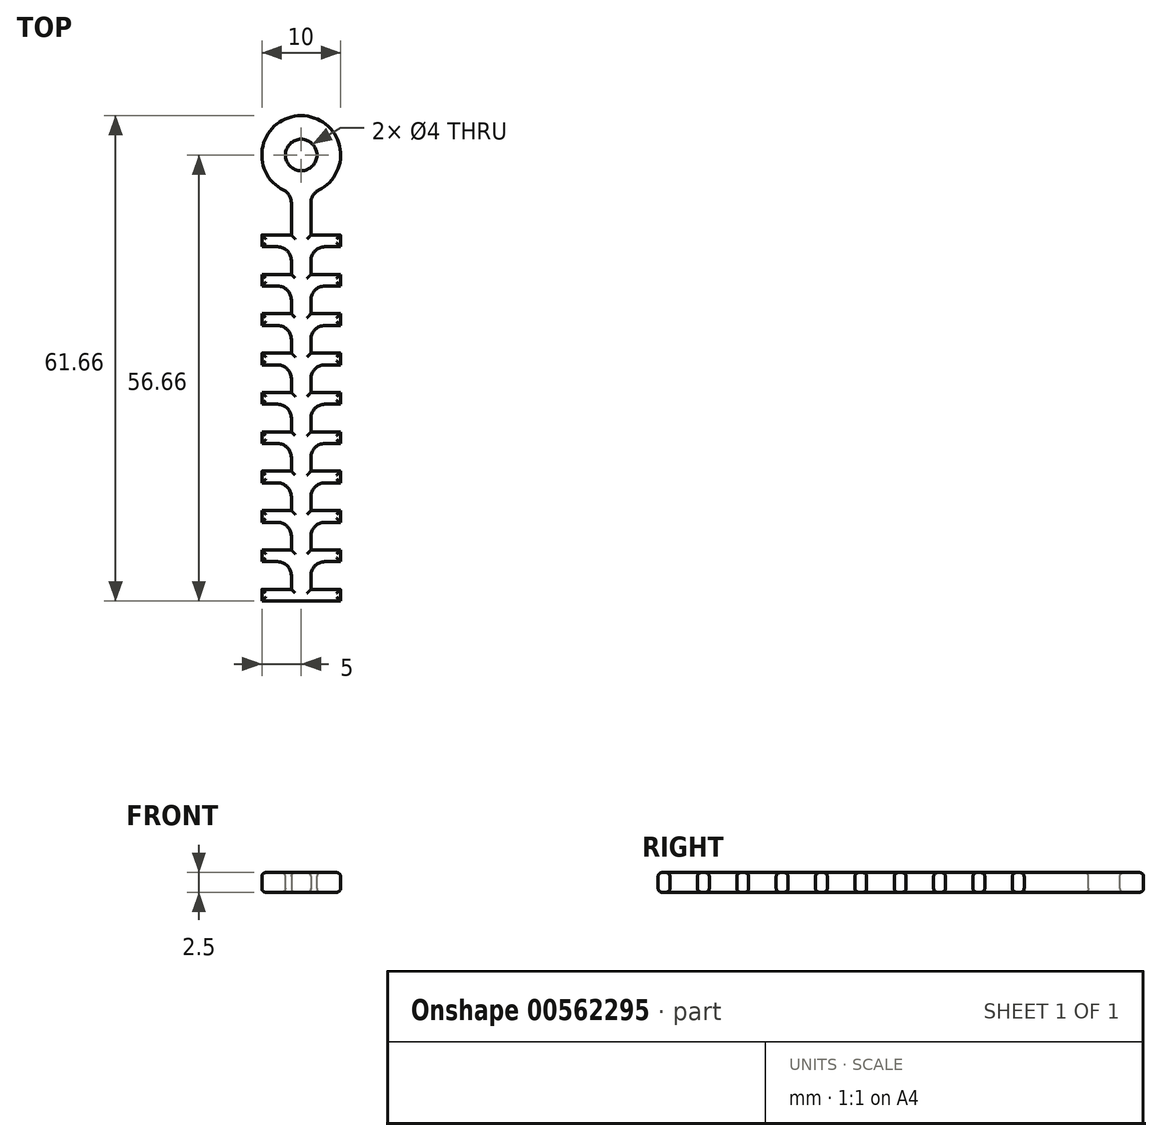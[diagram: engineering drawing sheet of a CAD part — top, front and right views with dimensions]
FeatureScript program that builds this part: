
annotation { "Feature Type Name" : "Feature", "Feature Type Description" : "" }
export const myFeature = defineFeature(function(context is Context, id is Id, definition is map)
    precondition{}
    {
        {
            var Q0;
            Q0=qCreatedBy(makeId("Top.planeOp"),FACE);
            var sketch = newSketch(context, id + "F0", { "sketchPlane" : qUnion([Q0])});
            skCircle(sketch, "E0", {"center": v(0, 0) * mm, "radius": 5 * mm});
            skLineSegment(sketch, "E1.bottom", {"start": v(5, -11.66) * mm, "end": v(-5, -11.66) * mm});
            skLineSegment(sketch, "E1.top", {"start": v(5, -10.16) * mm, "end": v(-5, -10.16) * mm});
            skLineSegment(sketch, "E1.left", {"start": v(5, -11.66) * mm, "end": v(5, -10.16) * mm});
            skLineSegment(sketch, "E1.right", {"start": v(-5, -11.66) * mm, "end": v(-5, -10.16) * mm});
            skPoint(sketch, "E1.middle", {"position": v(0, -10.91) * mm});
            skPoint(sketch, "E2.0.1.0", {"position": v(0, -15.91) * mm});
            skLineSegment(sketch, "E2.0.1.1", {"start": v(-5, -16.66) * mm, "end": v(-5, -15.16) * mm});
            skLineSegment(sketch, "E2.0.1.2", {"start": v(5, -16.66) * mm, "end": v(5, -15.16) * mm});
            skLineSegment(sketch, "E2.0.1.3", {"start": v(5, -15.16) * mm, "end": v(-5, -15.16) * mm});
            skLineSegment(sketch, "E2.0.1.4", {"start": v(5, -16.66) * mm, "end": v(-5, -16.66) * mm});
            skPoint(sketch, "E2.0.2.0", {"position": v(0, -20.91) * mm});
            skLineSegment(sketch, "E2.0.2.1", {"start": v(-5, -21.66) * mm, "end": v(-5, -20.16) * mm});
            skLineSegment(sketch, "E2.0.2.2", {"start": v(5, -21.66) * mm, "end": v(5, -20.16) * mm});
            skLineSegment(sketch, "E2.0.2.3", {"start": v(5, -20.16) * mm, "end": v(-5, -20.16) * mm});
            skLineSegment(sketch, "E2.0.2.4", {"start": v(5, -21.66) * mm, "end": v(-5, -21.66) * mm});
            skPoint(sketch, "E2.0.3.0", {"position": v(0, -25.91) * mm});
            skLineSegment(sketch, "E2.0.3.1", {"start": v(-5, -26.66) * mm, "end": v(-5, -25.16) * mm});
            skLineSegment(sketch, "E2.0.3.2", {"start": v(5, -26.66) * mm, "end": v(5, -25.16) * mm});
            skLineSegment(sketch, "E2.0.3.3", {"start": v(5, -25.16) * mm, "end": v(-5, -25.16) * mm});
            skLineSegment(sketch, "E2.0.3.4", {"start": v(5, -26.66) * mm, "end": v(-5, -26.66) * mm});
            skPoint(sketch, "E2.0.4.0", {"position": v(0, -30.91) * mm});
            skLineSegment(sketch, "E2.0.4.1", {"start": v(-5, -31.66) * mm, "end": v(-5, -30.16) * mm});
            skLineSegment(sketch, "E2.0.4.2", {"start": v(5, -31.66) * mm, "end": v(5, -30.16) * mm});
            skLineSegment(sketch, "E2.0.4.3", {"start": v(5, -30.16) * mm, "end": v(-5, -30.16) * mm});
            skLineSegment(sketch, "E2.0.4.4", {"start": v(5, -31.66) * mm, "end": v(-5, -31.66) * mm});
            skPoint(sketch, "E2.0.5.0", {"position": v(0, -35.91) * mm});
            skLineSegment(sketch, "E2.0.5.1", {"start": v(-5, -36.66) * mm, "end": v(-5, -35.16) * mm});
            skLineSegment(sketch, "E2.0.5.2", {"start": v(5, -36.66) * mm, "end": v(5, -35.16) * mm});
            skLineSegment(sketch, "E2.0.5.3", {"start": v(5, -35.16) * mm, "end": v(-5, -35.16) * mm});
            skLineSegment(sketch, "E2.0.5.4", {"start": v(5, -36.66) * mm, "end": v(-5, -36.66) * mm});
            skPoint(sketch, "E2.0.6.0", {"position": v(0, -40.91) * mm});
            skLineSegment(sketch, "E2.0.6.1", {"start": v(-5, -41.66) * mm, "end": v(-5, -40.16) * mm});
            skLineSegment(sketch, "E2.0.6.2", {"start": v(5, -41.66) * mm, "end": v(5, -40.16) * mm});
            skLineSegment(sketch, "E2.0.6.3", {"start": v(5, -40.16) * mm, "end": v(-5, -40.16) * mm});
            skLineSegment(sketch, "E2.0.6.4", {"start": v(5, -41.66) * mm, "end": v(-5, -41.66) * mm});
            skPoint(sketch, "E2.0.7.0", {"position": v(0, -45.91) * mm});
            skLineSegment(sketch, "E2.0.7.1", {"start": v(-5, -46.66) * mm, "end": v(-5, -45.16) * mm});
            skLineSegment(sketch, "E2.0.7.2", {"start": v(5, -46.66) * mm, "end": v(5, -45.16) * mm});
            skLineSegment(sketch, "E2.0.7.3", {"start": v(5, -45.16) * mm, "end": v(-5, -45.16) * mm});
            skLineSegment(sketch, "E2.0.7.4", {"start": v(5, -46.66) * mm, "end": v(-5, -46.66) * mm});
            skPoint(sketch, "E2.0.8.0", {"position": v(0, -50.91) * mm});
            skLineSegment(sketch, "E2.0.8.1", {"start": v(-5, -51.66) * mm, "end": v(-5, -50.16) * mm});
            skLineSegment(sketch, "E2.0.8.2", {"start": v(5, -51.66) * mm, "end": v(5, -50.16) * mm});
            skLineSegment(sketch, "E2.0.8.3", {"start": v(5, -50.16) * mm, "end": v(-5, -50.16) * mm});
            skLineSegment(sketch, "E2.0.8.4", {"start": v(5, -51.66) * mm, "end": v(-5, -51.66) * mm});
            skPoint(sketch, "E2.0.9.0", {"position": v(0, -55.91) * mm});
            skLineSegment(sketch, "E2.0.9.1", {"start": v(-5, -56.66) * mm, "end": v(-5, -55.16) * mm});
            skLineSegment(sketch, "E2.0.9.2", {"start": v(5, -56.66) * mm, "end": v(5, -55.16) * mm});
            skLineSegment(sketch, "E2.0.9.3", {"start": v(5, -55.16) * mm, "end": v(-5, -55.16) * mm});
            skLineSegment(sketch, "E2.0.9.4", {"start": v(5, -56.66) * mm, "end": v(-5, -56.66) * mm});
            skLineSegment(sketch, "E2.direction1", {"start": v(-5, -11.66) * mm, "end": v(12.1, -11.66) * mm, "construction": true});
            skLineSegment(sketch, "E2.direction2", {"start": v(-5, -11.66) * mm, "end": v(-5, -16.66) * mm, "construction": true});
            skLineSegment(sketch, "E3.bottom", {"start": v(-1.25, -55.16) * mm, "end": v(1.25, -55.16) * mm});
            skLineSegment(sketch, "E3.top", {"start": v(-1.25, -4.84) * mm, "end": v(1.25, -4.84) * mm});
            skLineSegment(sketch, "E3.left", {"start": v(-1.25, -55.16) * mm, "end": v(-1.25, -4.84) * mm});
            skLineSegment(sketch, "E3.right", {"start": v(1.25, -55.16) * mm, "end": v(1.25, -4.84) * mm});
            skSolve(sketch);
        }
        {
            var Q0;
            Q0 = qSketchRegion(id + "F0", true);
            extrude(context, id + "F1", {"entities" : qUnion([Q0]), "depth" : 2.5 * mm, "offsetDistance" : 25 * mm});
        }
        {
            var Q0;
            Q0=makeQuery(id+"F1.opExtrude","CAP_FACE",FACE,{"disambiguationData":[OSD([sQuery(id+"F0.wireOp",EDGE,"E0"),sQuery(id+"F0.wireOp",EDGE,"E1.bottom"),sQuery(id+"F0.wireOp",EDGE,"E1.top"),sQuery(id+"F0.wireOp",EDGE,"E1.left"),sQuery(id+"F0.wireOp",EDGE,"E1.right"),sQuery(id+"F0.wireOp",EDGE,"E2.0.1.1"),sQuery(id+"F0.wireOp",EDGE,"E2.0.1.2"),sQuery(id+"F0.wireOp",EDGE,"E2.0.1.3"),sQuery(id+"F0.wireOp",EDGE,"E2.0.1.4"),sQuery(id+"F0.wireOp",EDGE,"E2.0.2.1"),sQuery(id+"F0.wireOp",EDGE,"E2.0.2.2"),sQuery(id+"F0.wireOp",EDGE,"E2.0.2.3"),sQuery(id+"F0.wireOp",EDGE,"E2.0.2.4"),sQuery(id+"F0.wireOp",EDGE,"E2.0.3.1"),sQuery(id+"F0.wireOp",EDGE,"E2.0.3.2"),sQuery(id+"F0.wireOp",EDGE,"E2.0.3.3"),sQuery(id+"F0.wireOp",EDGE,"E2.0.3.4"),sQuery(id+"F0.wireOp",EDGE,"E2.0.4.1"),sQuery(id+"F0.wireOp",EDGE,"E2.0.4.2"),sQuery(id+"F0.wireOp",EDGE,"E2.0.4.3"),sQuery(id+"F0.wireOp",EDGE,"E2.0.4.4"),sQuery(id+"F0.wireOp",EDGE,"E2.0.5.1"),sQuery(id+"F0.wireOp",EDGE,"E2.0.5.2"),sQuery(id+"F0.wireOp",EDGE,"E2.0.5.3"),sQuery(id+"F0.wireOp",EDGE,"E2.0.5.4"),sQuery(id+"F0.wireOp",EDGE,"E2.0.6.1"),sQuery(id+"F0.wireOp",EDGE,"E2.0.6.2"),sQuery(id+"F0.wireOp",EDGE,"E2.0.6.3"),sQuery(id+"F0.wireOp",EDGE,"E2.0.6.4"),sQuery(id+"F0.wireOp",EDGE,"E2.0.7.1"),sQuery(id+"F0.wireOp",EDGE,"E2.0.7.2"),sQuery(id+"F0.wireOp",EDGE,"E2.0.7.3"),sQuery(id+"F0.wireOp",EDGE,"E2.0.7.4"),sQuery(id+"F0.wireOp",EDGE,"E2.0.8.1"),sQuery(id+"F0.wireOp",EDGE,"E2.0.8.2"),sQuery(id+"F0.wireOp",EDGE,"E2.0.8.3"),sQuery(id+"F0.wireOp",EDGE,"E2.0.8.4"),sQuery(id+"F0.wireOp",EDGE,"E2.0.9.1"),sQuery(id+"F0.wireOp",EDGE,"E2.0.9.2"),sQuery(id+"F0.wireOp",EDGE,"E2.0.9.3"),sQuery(id+"F0.wireOp",EDGE,"E2.0.9.4"),sQuery(id+"F0.wireOp",EDGE,"E3.left"),sQuery(id+"F0.wireOp",EDGE,"E3.right")])],"isStart":false});
            var sketch = newSketch(context, id + "F2", { "sketchPlane" : qUnion([Q0])});
            skCircle(sketch, "E4", {"center": v(0, 0) * mm, "radius": 2 * mm});
            skSolve(sketch);
        }
        {
            var Q0;
            Q0 = qSketchRegion(id + "F2", true);
            var Q1;
            Q1=makeQuery(id+"F1.opExtrude","CAP_FACE",FACE,{"disambiguationData":[OSD([sQuery(id+"F0.wireOp",EDGE,"E0"),sQuery(id+"F0.wireOp",EDGE,"E1.bottom"),sQuery(id+"F0.wireOp",EDGE,"E1.top"),sQuery(id+"F0.wireOp",EDGE,"E1.left"),sQuery(id+"F0.wireOp",EDGE,"E1.right"),sQuery(id+"F0.wireOp",EDGE,"E2.0.1.1"),sQuery(id+"F0.wireOp",EDGE,"E2.0.1.2"),sQuery(id+"F0.wireOp",EDGE,"E2.0.1.3"),sQuery(id+"F0.wireOp",EDGE,"E2.0.1.4"),sQuery(id+"F0.wireOp",EDGE,"E2.0.2.1"),sQuery(id+"F0.wireOp",EDGE,"E2.0.2.2"),sQuery(id+"F0.wireOp",EDGE,"E2.0.2.3"),sQuery(id+"F0.wireOp",EDGE,"E2.0.2.4"),sQuery(id+"F0.wireOp",EDGE,"E2.0.3.1"),sQuery(id+"F0.wireOp",EDGE,"E2.0.3.2"),sQuery(id+"F0.wireOp",EDGE,"E2.0.3.3"),sQuery(id+"F0.wireOp",EDGE,"E2.0.3.4"),sQuery(id+"F0.wireOp",EDGE,"E2.0.4.1"),sQuery(id+"F0.wireOp",EDGE,"E2.0.4.2"),sQuery(id+"F0.wireOp",EDGE,"E2.0.4.3"),sQuery(id+"F0.wireOp",EDGE,"E2.0.4.4"),sQuery(id+"F0.wireOp",EDGE,"E2.0.5.1"),sQuery(id+"F0.wireOp",EDGE,"E2.0.5.2"),sQuery(id+"F0.wireOp",EDGE,"E2.0.5.3"),sQuery(id+"F0.wireOp",EDGE,"E2.0.5.4"),sQuery(id+"F0.wireOp",EDGE,"E2.0.6.1"),sQuery(id+"F0.wireOp",EDGE,"E2.0.6.2"),sQuery(id+"F0.wireOp",EDGE,"E2.0.6.3"),sQuery(id+"F0.wireOp",EDGE,"E2.0.6.4"),sQuery(id+"F0.wireOp",EDGE,"E2.0.7.1"),sQuery(id+"F0.wireOp",EDGE,"E2.0.7.2"),sQuery(id+"F0.wireOp",EDGE,"E2.0.7.3"),sQuery(id+"F0.wireOp",EDGE,"E2.0.7.4"),sQuery(id+"F0.wireOp",EDGE,"E2.0.8.1"),sQuery(id+"F0.wireOp",EDGE,"E2.0.8.2"),sQuery(id+"F0.wireOp",EDGE,"E2.0.8.3"),sQuery(id+"F0.wireOp",EDGE,"E2.0.8.4"),sQuery(id+"F0.wireOp",EDGE,"E2.0.9.1"),sQuery(id+"F0.wireOp",EDGE,"E2.0.9.2"),sQuery(id+"F0.wireOp",EDGE,"E2.0.9.3"),sQuery(id+"F0.wireOp",EDGE,"E2.0.9.4"),sQuery(id+"F0.wireOp",EDGE,"E3.left"),sQuery(id+"F0.wireOp",EDGE,"E3.right")])],"isStart":true});
            extrude(context, id + "F3", {"entities" : qUnion([Q0]), "operationType" : NewBodyOperationType.REMOVE, "endBound" : BoundingType.UP_TO_SURFACE, "oppositeDirection" : true, "depth" : 25 * mm, "endBoundEntityFace" : qUnion([Q1]), "offsetDistance" : 25 * mm});
        }
        {
            var Q0;
            Q0=makeQuery(id+"F1.opExtrude","SWEPT_EDGE",EDGE,{"disambiguationData":[OSD([sQuery(id+"F0.wireOp",EDGE,"E0"),sQuery(id+"F0.wireOp",EDGE,"E3.top"),sQuery(id+"F0.wireOp",EDGE,"E3.right")])]});
            var Q1;
            Q1=makeQuery(id+"F1.opExtrude","SWEPT_EDGE",EDGE,{"disambiguationData":[OSD([sQuery(id+"F0.wireOp",EDGE,"E0"),sQuery(id+"F0.wireOp",EDGE,"E3.top"),sQuery(id+"F0.wireOp",EDGE,"E3.left")])]});
            var Q2;
            Q2=makeQuery(id+"F1.opExtrude","SWEPT_EDGE",EDGE,{"disambiguationData":[OSD([sQuery(id+"F0.wireOp",EDGE,"E1.bottom"),sQuery(id+"F0.wireOp",EDGE,"E3.right")])]});
            var Q3;
            Q3=makeQuery(id+"F1.opExtrude","SWEPT_EDGE",EDGE,{"disambiguationData":[OSD([sQuery(id+"F0.wireOp",EDGE,"E2.0.1.4"),sQuery(id+"F0.wireOp",EDGE,"E3.right")])]});
            var Q4;
            Q4=makeQuery(id+"F1.opExtrude","SWEPT_EDGE",EDGE,{"disambiguationData":[OSD([sQuery(id+"F0.wireOp",EDGE,"E2.0.2.4"),sQuery(id+"F0.wireOp",EDGE,"E3.right")])]});
            var Q5;
            Q5=makeQuery(id+"F1.opExtrude","SWEPT_EDGE",EDGE,{"disambiguationData":[OSD([sQuery(id+"F0.wireOp",EDGE,"E2.0.3.4"),sQuery(id+"F0.wireOp",EDGE,"E3.right")])]});
            var Q6;
            Q6=makeQuery(id+"F1.opExtrude","SWEPT_EDGE",EDGE,{"disambiguationData":[OSD([sQuery(id+"F0.wireOp",EDGE,"E2.0.4.4"),sQuery(id+"F0.wireOp",EDGE,"E3.right")])]});
            var Q7;
            Q7=makeQuery(id+"F1.opExtrude","SWEPT_EDGE",EDGE,{"disambiguationData":[OSD([sQuery(id+"F0.wireOp",EDGE,"E2.0.5.4"),sQuery(id+"F0.wireOp",EDGE,"E3.right")])]});
            var Q8;
            Q8=makeQuery(id+"F1.opExtrude","SWEPT_EDGE",EDGE,{"disambiguationData":[OSD([sQuery(id+"F0.wireOp",EDGE,"E2.0.6.4"),sQuery(id+"F0.wireOp",EDGE,"E3.right")])]});
            var Q9;
            Q9=makeQuery(id+"F1.opExtrude","SWEPT_EDGE",EDGE,{"disambiguationData":[OSD([sQuery(id+"F0.wireOp",EDGE,"E2.0.7.4"),sQuery(id+"F0.wireOp",EDGE,"E3.right")])]});
            var Q10;
            Q10=makeQuery(id+"F1.opExtrude","SWEPT_EDGE",EDGE,{"disambiguationData":[OSD([sQuery(id+"F0.wireOp",EDGE,"E2.0.8.4"),sQuery(id+"F0.wireOp",EDGE,"E3.right")])]});
            var Q11;
            Q11=makeQuery(id+"F1.opExtrude","SWEPT_EDGE",EDGE,{"disambiguationData":[OSD([sQuery(id+"F0.wireOp",EDGE,"E2.0.8.4"),sQuery(id+"F0.wireOp",EDGE,"E3.left")])]});
            var Q12;
            Q12=makeQuery(id+"F1.opExtrude","SWEPT_EDGE",EDGE,{"disambiguationData":[OSD([sQuery(id+"F0.wireOp",EDGE,"E2.0.7.4"),sQuery(id+"F0.wireOp",EDGE,"E3.left")])]});
            var Q13;
            Q13=makeQuery(id+"F1.opExtrude","SWEPT_EDGE",EDGE,{"disambiguationData":[OSD([sQuery(id+"F0.wireOp",EDGE,"E2.0.6.4"),sQuery(id+"F0.wireOp",EDGE,"E3.left")])]});
            var Q14;
            Q14=makeQuery(id+"F1.opExtrude","SWEPT_EDGE",EDGE,{"disambiguationData":[OSD([sQuery(id+"F0.wireOp",EDGE,"E2.0.5.4"),sQuery(id+"F0.wireOp",EDGE,"E3.left")])]});
            var Q15;
            Q15=makeQuery(id+"F1.opExtrude","SWEPT_EDGE",EDGE,{"disambiguationData":[OSD([sQuery(id+"F0.wireOp",EDGE,"E2.0.4.4"),sQuery(id+"F0.wireOp",EDGE,"E3.left")])]});
            var Q16;
            Q16=makeQuery(id+"F1.opExtrude","SWEPT_EDGE",EDGE,{"disambiguationData":[OSD([sQuery(id+"F0.wireOp",EDGE,"E2.0.3.4"),sQuery(id+"F0.wireOp",EDGE,"E3.left")])]});
            var Q17;
            Q17=makeQuery(id+"F1.opExtrude","SWEPT_EDGE",EDGE,{"disambiguationData":[OSD([sQuery(id+"F0.wireOp",EDGE,"E2.0.2.4"),sQuery(id+"F0.wireOp",EDGE,"E3.left")])]});
            var Q18;
            Q18=makeQuery(id+"F1.opExtrude","SWEPT_EDGE",EDGE,{"disambiguationData":[OSD([sQuery(id+"F0.wireOp",EDGE,"E2.0.1.4"),sQuery(id+"F0.wireOp",EDGE,"E3.left")])]});
            var Q19;
            Q19=makeQuery(id+"F1.opExtrude","SWEPT_EDGE",EDGE,{"disambiguationData":[OSD([sQuery(id+"F0.wireOp",EDGE,"E1.bottom"),sQuery(id+"F0.wireOp",EDGE,"E3.left")])]});
            fillet(context, id + "F4", {"entities" : qUnion([Q0, Q1, Q2, Q3, Q4, Q5, Q6, Q7, Q8, Q9, Q10, Q11, Q12, Q13, Q14, Q15, Q16, Q17, Q18, Q19]), "radius" : 1.75 * mm, "tangentPropagation" : true, "allowEdgeOverflow" : false});
        }
        {
            var Q0;
            Q0=makeQuery(id+"F1.opExtrude","CAP_FACE",FACE,{"disambiguationData":[OSD([sQuery(id+"F0.wireOp",EDGE,"E0"),sQuery(id+"F0.wireOp",EDGE,"E1.bottom"),sQuery(id+"F0.wireOp",EDGE,"E1.top"),sQuery(id+"F0.wireOp",EDGE,"E1.left"),sQuery(id+"F0.wireOp",EDGE,"E1.right"),sQuery(id+"F0.wireOp",EDGE,"E2.0.1.1"),sQuery(id+"F0.wireOp",EDGE,"E2.0.1.2"),sQuery(id+"F0.wireOp",EDGE,"E2.0.1.3"),sQuery(id+"F0.wireOp",EDGE,"E2.0.1.4"),sQuery(id+"F0.wireOp",EDGE,"E2.0.2.1"),sQuery(id+"F0.wireOp",EDGE,"E2.0.2.2"),sQuery(id+"F0.wireOp",EDGE,"E2.0.2.3"),sQuery(id+"F0.wireOp",EDGE,"E2.0.2.4"),sQuery(id+"F0.wireOp",EDGE,"E2.0.3.1"),sQuery(id+"F0.wireOp",EDGE,"E2.0.3.2"),sQuery(id+"F0.wireOp",EDGE,"E2.0.3.3"),sQuery(id+"F0.wireOp",EDGE,"E2.0.3.4"),sQuery(id+"F0.wireOp",EDGE,"E2.0.4.1"),sQuery(id+"F0.wireOp",EDGE,"E2.0.4.2"),sQuery(id+"F0.wireOp",EDGE,"E2.0.4.3"),sQuery(id+"F0.wireOp",EDGE,"E2.0.4.4"),sQuery(id+"F0.wireOp",EDGE,"E2.0.5.1"),sQuery(id+"F0.wireOp",EDGE,"E2.0.5.2"),sQuery(id+"F0.wireOp",EDGE,"E2.0.5.3"),sQuery(id+"F0.wireOp",EDGE,"E2.0.5.4"),sQuery(id+"F0.wireOp",EDGE,"E2.0.6.1"),sQuery(id+"F0.wireOp",EDGE,"E2.0.6.2"),sQuery(id+"F0.wireOp",EDGE,"E2.0.6.3"),sQuery(id+"F0.wireOp",EDGE,"E2.0.6.4"),sQuery(id+"F0.wireOp",EDGE,"E2.0.7.1"),sQuery(id+"F0.wireOp",EDGE,"E2.0.7.2"),sQuery(id+"F0.wireOp",EDGE,"E2.0.7.3"),sQuery(id+"F0.wireOp",EDGE,"E2.0.7.4"),sQuery(id+"F0.wireOp",EDGE,"E2.0.8.1"),sQuery(id+"F0.wireOp",EDGE,"E2.0.8.2"),sQuery(id+"F0.wireOp",EDGE,"E2.0.8.3"),sQuery(id+"F0.wireOp",EDGE,"E2.0.8.4"),sQuery(id+"F0.wireOp",EDGE,"E2.0.9.1"),sQuery(id+"F0.wireOp",EDGE,"E2.0.9.2"),sQuery(id+"F0.wireOp",EDGE,"E2.0.9.3"),sQuery(id+"F0.wireOp",EDGE,"E2.0.9.4"),sQuery(id+"F0.wireOp",EDGE,"E3.left"),sQuery(id+"F0.wireOp",EDGE,"E3.right")])],"isStart":false});
            fillet(context, id + "F5", {"entities" : qUnion([Q0]), "radius" : .5 * mm, "tangentPropagation" : true, "allowEdgeOverflow" : false});
        }
        {
            var Q0;
            Q0=makeQuery(id+"F1.opExtrude","CAP_FACE",FACE,{"disambiguationData":[OSD([sQuery(id+"F0.wireOp",EDGE,"E0"),sQuery(id+"F0.wireOp",EDGE,"E1.bottom"),sQuery(id+"F0.wireOp",EDGE,"E1.top"),sQuery(id+"F0.wireOp",EDGE,"E1.left"),sQuery(id+"F0.wireOp",EDGE,"E1.right"),sQuery(id+"F0.wireOp",EDGE,"E2.0.1.1"),sQuery(id+"F0.wireOp",EDGE,"E2.0.1.2"),sQuery(id+"F0.wireOp",EDGE,"E2.0.1.3"),sQuery(id+"F0.wireOp",EDGE,"E2.0.1.4"),sQuery(id+"F0.wireOp",EDGE,"E2.0.2.1"),sQuery(id+"F0.wireOp",EDGE,"E2.0.2.2"),sQuery(id+"F0.wireOp",EDGE,"E2.0.2.3"),sQuery(id+"F0.wireOp",EDGE,"E2.0.2.4"),sQuery(id+"F0.wireOp",EDGE,"E2.0.3.1"),sQuery(id+"F0.wireOp",EDGE,"E2.0.3.2"),sQuery(id+"F0.wireOp",EDGE,"E2.0.3.3"),sQuery(id+"F0.wireOp",EDGE,"E2.0.3.4"),sQuery(id+"F0.wireOp",EDGE,"E2.0.4.1"),sQuery(id+"F0.wireOp",EDGE,"E2.0.4.2"),sQuery(id+"F0.wireOp",EDGE,"E2.0.4.3"),sQuery(id+"F0.wireOp",EDGE,"E2.0.4.4"),sQuery(id+"F0.wireOp",EDGE,"E2.0.5.1"),sQuery(id+"F0.wireOp",EDGE,"E2.0.5.2"),sQuery(id+"F0.wireOp",EDGE,"E2.0.5.3"),sQuery(id+"F0.wireOp",EDGE,"E2.0.5.4"),sQuery(id+"F0.wireOp",EDGE,"E2.0.6.1"),sQuery(id+"F0.wireOp",EDGE,"E2.0.6.2"),sQuery(id+"F0.wireOp",EDGE,"E2.0.6.3"),sQuery(id+"F0.wireOp",EDGE,"E2.0.6.4"),sQuery(id+"F0.wireOp",EDGE,"E2.0.7.1"),sQuery(id+"F0.wireOp",EDGE,"E2.0.7.2"),sQuery(id+"F0.wireOp",EDGE,"E2.0.7.3"),sQuery(id+"F0.wireOp",EDGE,"E2.0.7.4"),sQuery(id+"F0.wireOp",EDGE,"E2.0.8.1"),sQuery(id+"F0.wireOp",EDGE,"E2.0.8.2"),sQuery(id+"F0.wireOp",EDGE,"E2.0.8.3"),sQuery(id+"F0.wireOp",EDGE,"E2.0.8.4"),sQuery(id+"F0.wireOp",EDGE,"E2.0.9.1"),sQuery(id+"F0.wireOp",EDGE,"E2.0.9.2"),sQuery(id+"F0.wireOp",EDGE,"E2.0.9.3"),sQuery(id+"F0.wireOp",EDGE,"E2.0.9.4"),sQuery(id+"F0.wireOp",EDGE,"E3.left"),sQuery(id+"F0.wireOp",EDGE,"E3.right")])],"isStart":true});
            fillet(context, id + "F6", {"entities" : qUnion([Q0]), "radius" : .5 * mm, "tangentPropagation" : true, "allowEdgeOverflow" : false});
        }
    });
